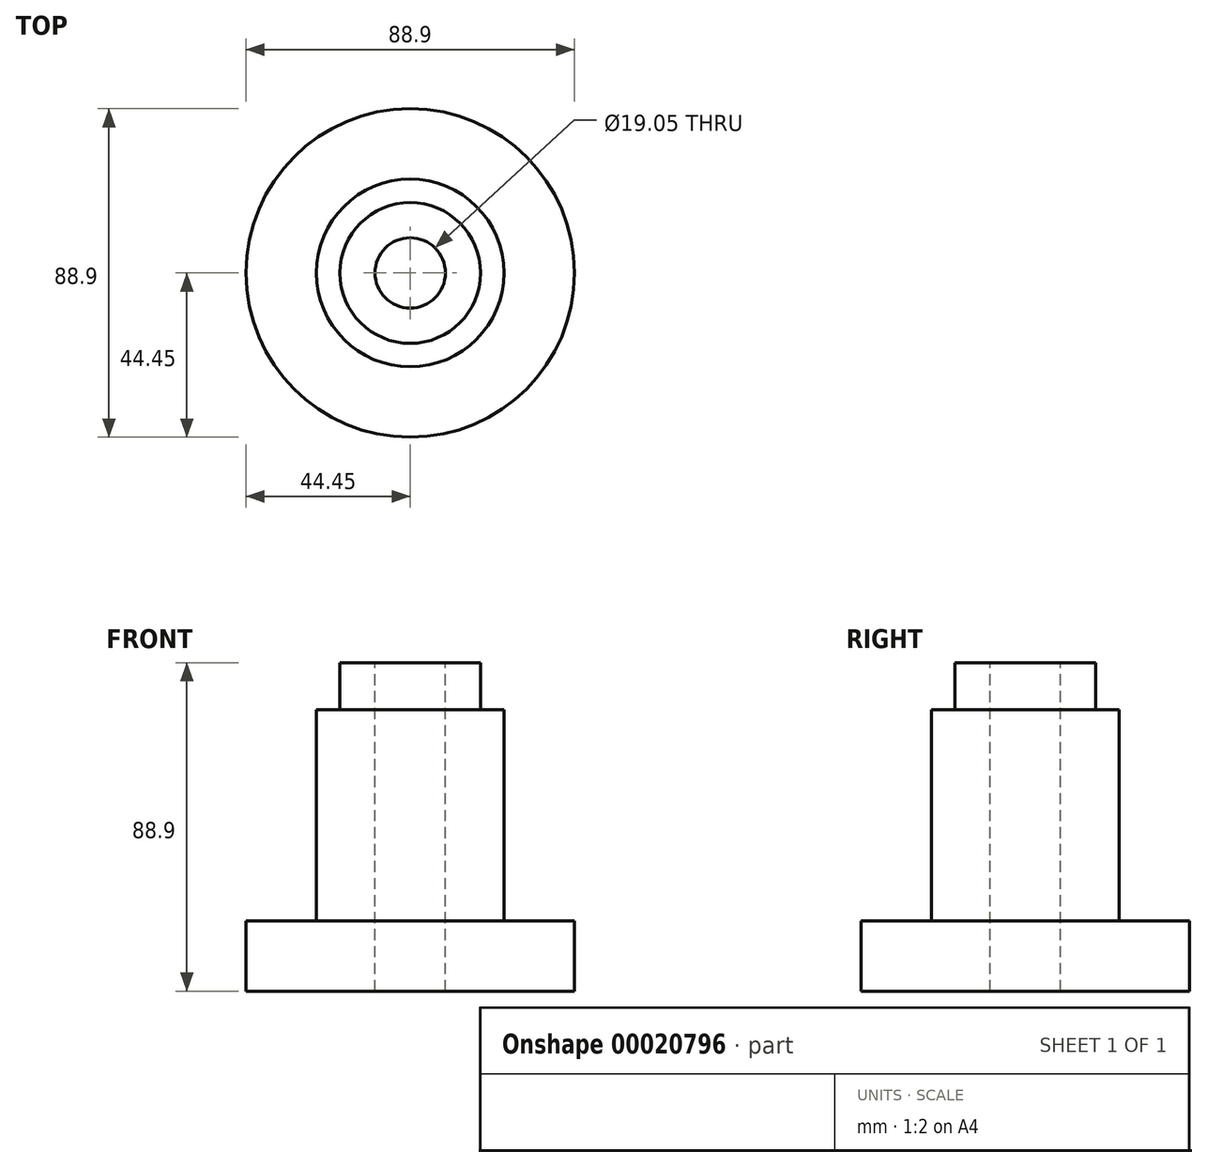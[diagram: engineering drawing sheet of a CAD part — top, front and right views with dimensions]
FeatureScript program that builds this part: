
annotation { "Feature Type Name" : "Feature", "Feature Type Description" : "" }
export const myFeature = defineFeature(function(context is Context, id is Id, definition is map)
    precondition{}
    {
        {
            var Q0;
            Q0=qCreatedBy(makeId("Front.planeOp"),FACE);
            var sketch = newSketch(context, id + "F0", { "sketchPlane" : qUnion([Q0])});
            skLineSegment(sketch, "E0", {"start": v(-24.7, 5.23) * mm, "end": v(-24.7, -83.67) * mm});
            skLineSegment(sketch, "E1", {"start": v(-24.7, 5.23) * mm, "end": v(-5.66, 5.23) * mm});
            skLineSegment(sketch, "E2", {"start": v(-5.66, 5.23) * mm, "end": v(-5.66, -7.47) * mm});
            skLineSegment(sketch, "E3", {"start": v(-5.66, -7.47) * mm, "end": v(0.7, -7.47) * mm});
            skLineSegment(sketch, "E4", {"start": v(0.7, -7.47) * mm, "end": v(0.7, -64.62) * mm});
            skLineSegment(sketch, "E5", {"start": v(0.7, -64.62) * mm, "end": v(19.74, -64.62) * mm});
            skLineSegment(sketch, "E6", {"start": v(19.74, -64.62) * mm, "end": v(19.74, -83.67) * mm});
            skLineSegment(sketch, "E7", {"start": v(19.74, -83.67) * mm, "end": v(-24.7, -83.67) * mm});
            skSolve(sketch);
        }
        {
            var Q0;
            Q0=makeQuery(id+"F0.imprint","IMPRINT",FACE,{"disambiguationData":[TD([[makeQuery(id+"F0.imprint","IMPRINT",EDGE,{"derivedFrom":sQuery(id+"F0.wireOp",EDGE,"E0")}),1.0]])]});
            var Q1;
            Q1=sQuery(id+"F0.wireOp",EDGE,"E0");
            revolve(context, id + "F1", {"entities" : qUnion([Q0]), "axis" : qUnion([Q1]), "revolveType" : RevolveType.FULL});
        }
        {
            var Q0;
            Q0=makeQuery(id+"F1.opRevolve","SWEPT_FACE",FACE,{"disambiguationData":[OSD([sQuery(id+"F0.wireOp",EDGE,"E1")])]});
            var sketch = newSketch(context, id + "F2", { "sketchPlane" : qUnion([Q0])});
            skCircle(sketch, "E8", {"center": v(-24.7, 0) * mm, "radius": 9.53 * mm});
            skSolve(sketch);
        }
        {
            var Q0;
            Q0=makeQuery(id+"F2.imprint","IMPRINT",FACE,{"disambiguationData":[TD([[makeQuery(id+"F2.imprint","IMPRINT",EDGE,{"derivedFrom":sQuery(id+"F2.wireOp",EDGE,"E8")}),1.0]])]});
            extrude(context, id + "F3", {"entities" : qUnion([Q0]), "operationType" : NewBodyOperationType.REMOVE, "endBound" : BoundingType.THROUGH_ALL, "oppositeDirection" : true, "depth" : 25.4 * mm});
        }
    });
